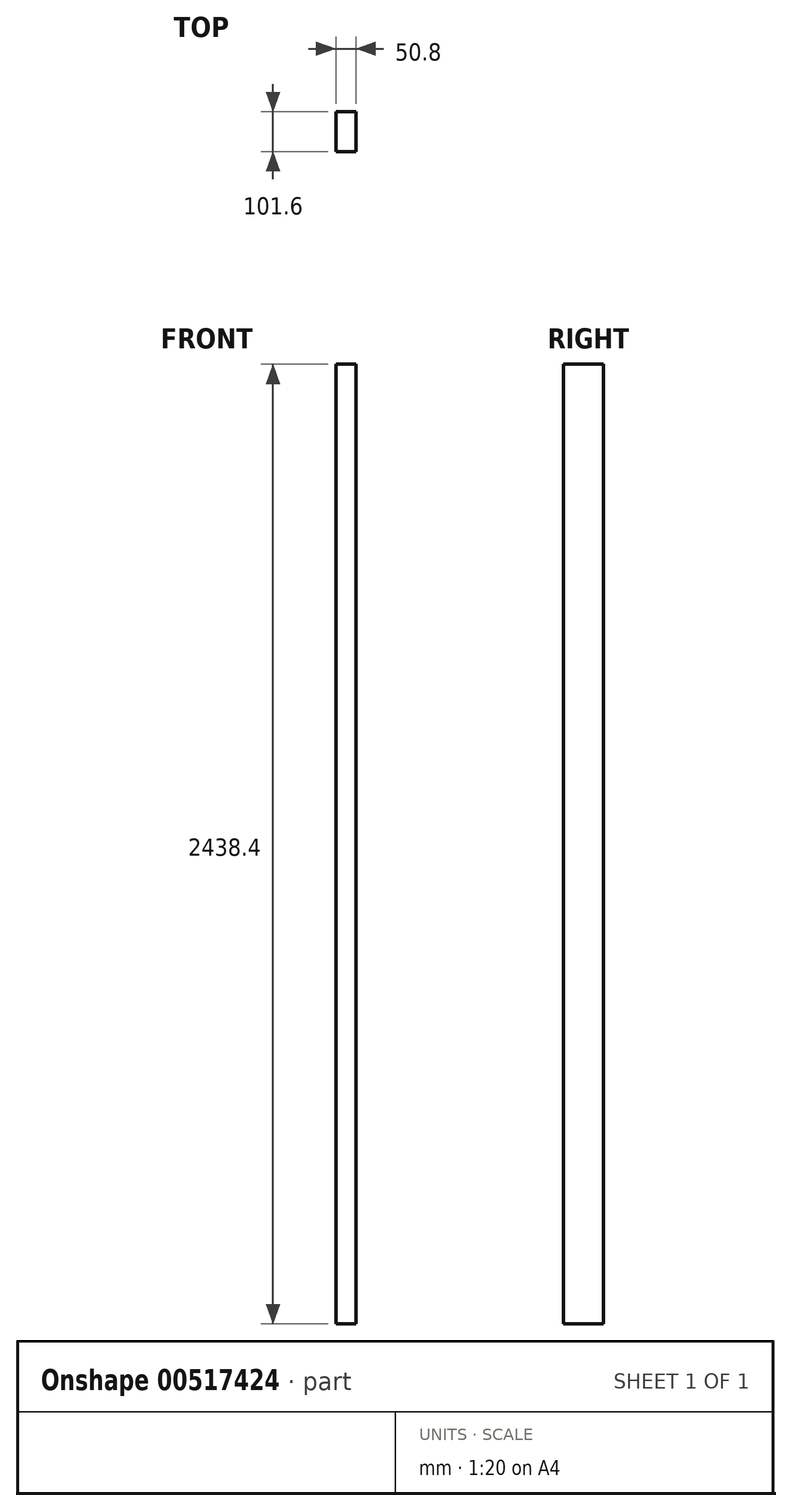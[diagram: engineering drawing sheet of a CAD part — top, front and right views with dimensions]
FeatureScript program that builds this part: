
annotation { "Feature Type Name" : "Feature", "Feature Type Description" : "" }
export const myFeature = defineFeature(function(context is Context, id is Id, definition is map)
    precondition{}
    {
        {
            var Q0;
            Q0=qCreatedBy(makeId("Front.planeOp"),FACE);
            var sketch = newSketch(context, id + "F0", { "sketchPlane" : qUnion([Q0])});
            skLineSegment(sketch, "E0.bottom", {"start": v(-117.67, 2341.51) * mm, "end": v(-66.87, 2341.51) * mm});
            skLineSegment(sketch, "E0.top", {"start": v(-117.67, -96.89) * mm, "end": v(-66.87, -96.89) * mm});
            skLineSegment(sketch, "E0.left", {"start": v(-117.67, 2341.51) * mm, "end": v(-117.67, -96.89) * mm});
            skLineSegment(sketch, "E0.right", {"start": v(-66.87, 2341.51) * mm, "end": v(-66.87, -96.89) * mm});
            skSolve(sketch);
        }
        {
            var Q0;
            Q0=makeQuery(id+"F0.imprint","IMPRINT",FACE,{"disambiguationData":[TD([[makeQuery(id+"F0.imprint","IMPRINT",EDGE,{"derivedFrom":sQuery(id+"F0.wireOp",EDGE,"E0.bottom")}),-1.0]])]});
            extrude(context, id + "F1", {"entities" : qUnion([Q0]), "depth" : 101.6 * mm, "offsetDistance" : 25.4 * mm});
        }
    });
